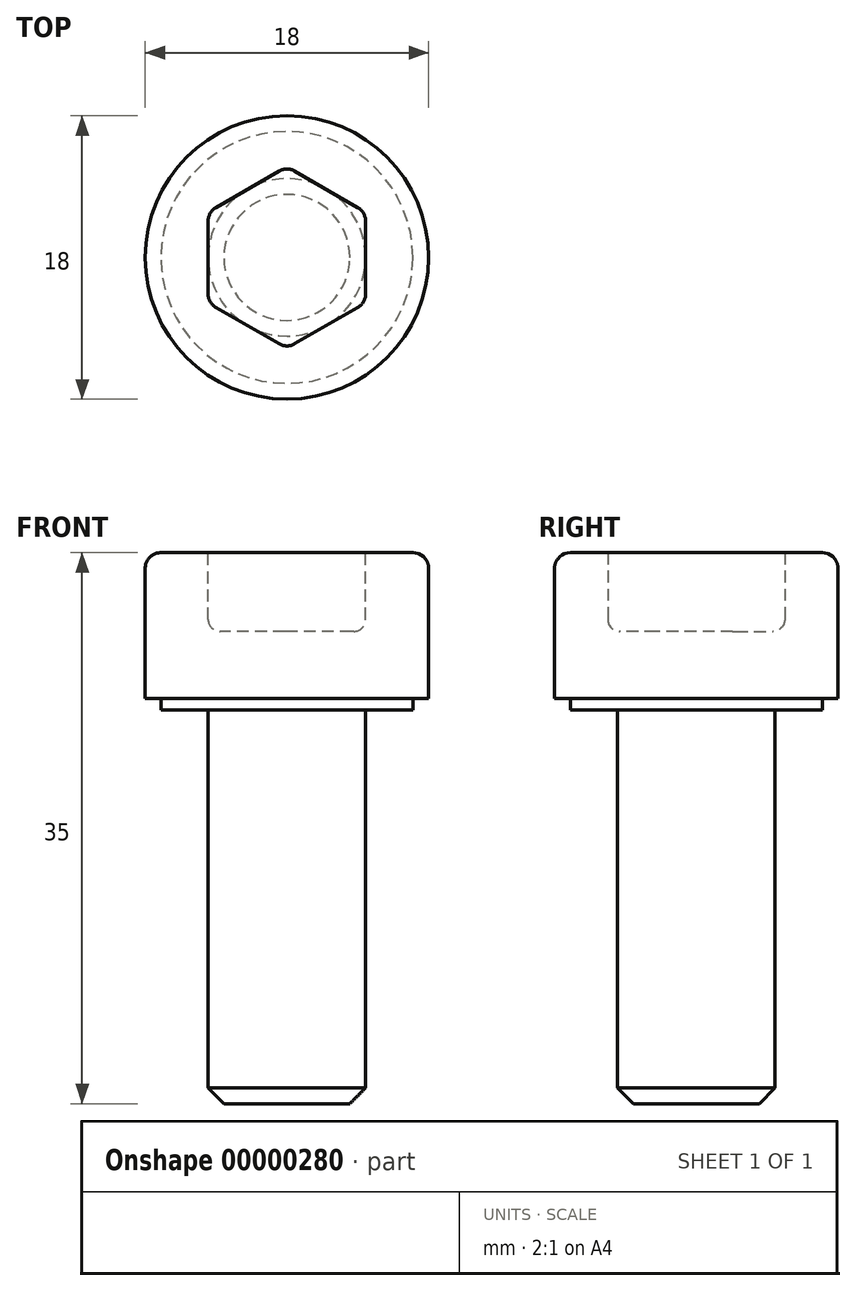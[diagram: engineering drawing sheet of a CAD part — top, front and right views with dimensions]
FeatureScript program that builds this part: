
annotation { "Feature Type Name" : "Feature", "Feature Type Description" : "" }
export const myFeature = defineFeature(function(context is Context, id is Id, definition is map)
    precondition{}
    {
        {
            var Q0;
            Q0=qCreatedBy(makeId("Front.planeOp"),FACE);
            var sketch = newSketch(context, id + "F0", { "sketchPlane" : qUnion([Q0])});
            skLineSegment(sketch, "E0", {"start": v(-5, 0) * mm, "end": v(-8, 0) * mm});
            skLineSegment(sketch, "E1", {"start": v(-8, 0) * mm, "end": v(-8, 0.75) * mm});
            skLineSegment(sketch, "E2", {"start": v(-8, 0.75) * mm, "end": v(-9, 0.75) * mm});
            skLineSegment(sketch, "E3", {"start": v(-9, 0.75) * mm, "end": v(-9, 10) * mm});
            skLineSegment(sketch, "E4", {"start": v(-9, 10) * mm, "end": v(0, 10) * mm});
            skLineSegment(sketch, "E5", {"start": v(0, 10) * mm, "end": v(0, -25) * mm});
            skLineSegment(sketch, "E6", {"start": v(0, -25) * mm, "end": v(-5, -25) * mm});
            skLineSegment(sketch, "E7", {"start": v(-5, -25) * mm, "end": v(-5, 0) * mm});
            skLineSegment(sketch, "E8", {"start": v(0, -25) * mm, "end": v(0, -26.5) * mm, "construction": true});
            skLineSegment(sketch, "E9.0.MirrorCS", {"start": v(0, -25) * mm, "end": v(5, -25) * mm, "construction": true});
            skLineSegment(sketch, "E10.0.MirrorCS", {"start": v(5, -25) * mm, "end": v(5, 0) * mm, "construction": true});
            skLineSegment(sketch, "E11.0.MirrorCS", {"start": v(5, 0) * mm, "end": v(8, 0) * mm, "construction": true});
            skLineSegment(sketch, "E12.0.MirrorCS", {"start": v(8, 0) * mm, "end": v(8, 0.75) * mm, "construction": true});
            skLineSegment(sketch, "E13.0.MirrorCS", {"start": v(8, 0.75) * mm, "end": v(9, 0.75) * mm, "construction": true});
            skLineSegment(sketch, "E14.0.MirrorCS", {"start": v(9, 0.75) * mm, "end": v(9, 10) * mm, "construction": true});
            skLineSegment(sketch, "E15.0.MirrorCS", {"start": v(9, 10) * mm, "end": v(0, 10) * mm, "construction": true});
            skSolve(sketch);
        }
        {
            var Q0;
            Q0=makeQuery(id+"F0.imprint","IMPRINT",FACE,{"disambiguationData":[TD([[makeQuery(id+"F0.imprint","IMPRINT",EDGE,{"derivedFrom":sQuery(id+"F0.wireOp",EDGE,"E0")}),-1.0]])]});
            var Q1;
            Q1=sQuery(id+"F0.wireOp",EDGE,"E5");
            revolve(context, id + "F1", {"entities" : qUnion([Q0]), "axis" : qUnion([Q1]), "revolveType" : RevolveType.FULL});
        }
        {
            var Q0;
            Q0=makeQuery(id+"F1.opRevolve","SWEPT_FACE",FACE,{"disambiguationData":[OSD([sQuery(id+"F0.wireOp",EDGE,"E4")])]});
            var sketch = newSketch(context, id + "F2", { "sketchPlane" : qUnion([Q0])});
            skCircle(sketch, "E16", {"center": v(0, 0) * mm, "radius": 5.77 * mm, "construction": true});
            skLineSegment(sketch, "E17", {"start": v(0, 5.77) * mm, "end": v(-5, 2.89) * mm});
            skLineSegment(sketch, "E18", {"start": v(-5, 2.89) * mm, "end": v(-5, -2.89) * mm});
            skLineSegment(sketch, "E19", {"start": v(-5, -2.89) * mm, "end": v(0, -5.77) * mm});
            skLineSegment(sketch, "E20", {"start": v(0, -5.77) * mm, "end": v(5, -2.89) * mm});
            skLineSegment(sketch, "E21", {"start": v(5, -2.89) * mm, "end": v(5, 2.89) * mm});
            skLineSegment(sketch, "E22", {"start": v(5, 2.89) * mm, "end": v(0, 5.77) * mm});
            skSolve(sketch);
        }
        {
            var Q0;
            Q0=makeQuery(id+"F2.imprint","IMPRINT",FACE,{"disambiguationData":[TD([[makeQuery(id+"F2.imprint","IMPRINT",EDGE,{"derivedFrom":sQuery(id+"F2.wireOp",EDGE,"E17")}),1.0]])]});
            extrude(context, id + "F3", {"entities" : qUnion([Q0]), "operationType" : NewBodyOperationType.REMOVE, "oppositeDirection" : true, "depth" : 5 * mm});
        }
        {
            var Q0;
            Q0=makeQuery(id+"F1.opRevolve","SWEPT_EDGE",EDGE,{"disambiguationData":[OSD([sQuery(id+"F0.wireOp",EDGE,"E3"),sQuery(id+"F0.wireOp",EDGE,"E4")])]});
            fillet(context, id + "F4", {"entities" : qUnion([Q0]), "radius" : 1 * mm, "tangentPropagation" : true, "allowEdgeOverflow" : false});
        }
        {
            var Q0;
            Q0=makeQuery(id+"F1.opRevolve","SWEPT_EDGE",EDGE,{"disambiguationData":[OSD([sQuery(id+"F0.wireOp",EDGE,"E6"),sQuery(id+"F0.wireOp",EDGE,"E7")])]});
            chamfer(context, id + "F5", {"entities" : qUnion([Q0]), "width" : 1 * mm, "tangentPropagation" : true});
        }
        {
            var Q0;
            Q0=makeQuery(id+"F3.boolean.opBoolean","COPY",EDGE,{"derivedFrom":makeQuery(id+"F3.opExtrude","SWEPT_EDGE",EDGE,{"disambiguationData":[OSD([sQuery(id+"F2.wireOp",EDGE,"E17"),sQuery(id+"F2.wireOp",EDGE,"E22")])]})});
            var Q1;
            Q1=makeQuery(id+"F3.boolean.opBoolean","COPY",EDGE,{"derivedFrom":makeQuery(id+"F3.opExtrude","SWEPT_EDGE",EDGE,{"disambiguationData":[OSD([sQuery(id+"F2.wireOp",EDGE,"E17"),sQuery(id+"F2.wireOp",EDGE,"E18")])]})});
            var Q2;
            Q2=makeQuery(id+"F3.boolean.opBoolean","COPY",EDGE,{"derivedFrom":makeQuery(id+"F3.opExtrude","SWEPT_EDGE",EDGE,{"disambiguationData":[OSD([sQuery(id+"F2.wireOp",EDGE,"E18"),sQuery(id+"F2.wireOp",EDGE,"E19")])]})});
            var Q3;
            Q3=makeQuery(id+"F3.boolean.opBoolean","COPY",EDGE,{"derivedFrom":makeQuery(id+"F3.opExtrude","SWEPT_EDGE",EDGE,{"disambiguationData":[OSD([sQuery(id+"F2.wireOp",EDGE,"E19"),sQuery(id+"F2.wireOp",EDGE,"E20")])]})});
            var Q4;
            Q4=makeQuery(id+"F3.boolean.opBoolean","COPY",EDGE,{"derivedFrom":makeQuery(id+"F3.opExtrude","SWEPT_EDGE",EDGE,{"disambiguationData":[OSD([sQuery(id+"F2.wireOp",EDGE,"E20"),sQuery(id+"F2.wireOp",EDGE,"E21")])]})});
            var Q5;
            Q5=makeQuery(id+"F3.boolean.opBoolean","COPY",EDGE,{"derivedFrom":makeQuery(id+"F3.opExtrude","SWEPT_EDGE",EDGE,{"disambiguationData":[OSD([sQuery(id+"F2.wireOp",EDGE,"E21"),sQuery(id+"F2.wireOp",EDGE,"E22")])]})});
            fillet(context, id + "F6", {"entities" : qUnion([Q0, Q1, Q2, Q3, Q4, Q5]), "radius" : 1 * mm, "tangentPropagation" : true, "allowEdgeOverflow" : false});
        }
        {
            var Q0;
            Q0=makeQuery(id+"F3.boolean.opBoolean","COPY",FACE,{"derivedFrom":makeQuery(id+"F3.opExtrude","CAP_FACE",FACE,{"disambiguationData":[OSD([sQuery(id+"F2.wireOp",EDGE,"E17"),sQuery(id+"F2.wireOp",EDGE,"E18"),sQuery(id+"F2.wireOp",EDGE,"E19"),sQuery(id+"F2.wireOp",EDGE,"E20"),sQuery(id+"F2.wireOp",EDGE,"E21"),sQuery(id+"F2.wireOp",EDGE,"E22")])],"isStart":false})});
            fillet(context, id + "F7", {"entities" : qUnion([Q0]), "radius" : 0.75 * mm, "tangentPropagation" : true, "allowEdgeOverflow" : false});
        }
    });
